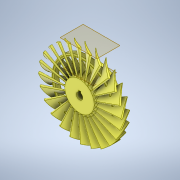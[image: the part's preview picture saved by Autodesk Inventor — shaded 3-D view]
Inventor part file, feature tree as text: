
AUTODESK INVENTOR PART (.ipt)
format: ipt  version: 2021.2 (Build 252289000, 289)  size: 3,381,760 bytes
history: native  units: in
note: dims shown in document units (in); Inventor stores cm internally (conversion verified against a paired STEP export)
features: sketch x6, extrude x4, plane x2, loft x1, pattern_circular x1, revolve x1, other x1
ambient origin geometry x8: Origin, YZ Plane, XZ Plane, XY Plane, X Axis, Y Axis, Z Axis, Center Point
bodies: Solid1 (feature_tree)
feature tree (16):
  extrude  "Extrusion1"  Depth=1.0in
  plane  "Work Plane1"
  plane  "Work Plane2"
  sketch  "Sketch5"  dims[d4=0.8in d15=2.0in]
  sketch  "Sketch6"  dims[d39=0.315in d40=0.125in]
  extrude  "Extrusion5"  Depth=2.0in
  sketch  "Sketch13"  dims[d66=3.9375in]
  extrude  "Extrusion7"  Depth=0.125in
  loft  "Loft5"
  pattern_circular  "Circular Pattern6"  [2 undecoded]
  revolve  "Revolution5"  [1 undecoded]
  extrude  "Extrusion8"  Depth=0.0625in
  sketch  "Sketch1"  dims[d0=1.4in d1=1.0in d2=0.0777in]
  sketch  "Sketch8"  dims[d41=0.125in d42=0.0in d43=0.0in]
  other  "Edges5"
  sketch  "Sketch14"  dims[d69=0.2in d70=0.0in d75=0.0312in d76=0.0625in d82=0.0625in d83=0.0in d84=90.0deg d85=0.0in d86=90.0deg d87=9.4488in d88=360.0deg d90=0.3in d91=0.125in d92=0.5in d93=0.05in d94=0.0in d95=90.0deg d96=0.0in d97=0.0in]
note: 3 required parameter values undecoded (feature->parameter linkage not recoverable at this tier; creation-order binding heuristic only, values carry confidence <= 0.55)